# Revit family: QF_ELECTROLUXPROFESSIONAL_586243_PUET10KVEO
name_source: partatom
category: Specialty Equipment
revit_build: Autodesk Revit 2018 (Build: 20190510_1515(x64)
units: mm (PartAtom-declared; Revit-internal decimal feet)

## family parameters
Always vertical = Yes
Cut with Voids When Loaded = No
Part Type = Normal
Room Calculation Point = No
Round Connector Dimension = Use Radius
Shared = Yes
Work Plane-Based = No

## types (6) — shared parameters
50 Hertz Option = No
60 Hertz Option = Yes
Apparent Power = 0 VA
Cold Water Connection Height = 395 mm  [stored 1.29593 ft]
Cold Water Radius Size = 6.35 mm  [stored 0.0208333 ft]
Cold Water Size = 1"
Conn Conduit = Yes
Cycle = 60 Hz
Depth = 900 mm  [stored 2.95276 ft]
Direct Waste Size = 1"
Elec Conn Connection Height = 450 mm  [stored 1.47638 ft]
Electrical Remarks = 3PH+N 50/60HZ COMPATIBLE
FL Amps = 0 A
HP = 27.6 HP
Height = 900 mm  [stored 2.95276 ft]
Hot Water Connection Height = 395 mm  [stored 1.29593 ft]
Hot Water Flow = 0 GPM
Hot Water Radius Size = 6.35 mm  [stored 0.0208333 ft]
Hot Water Size = 1"
Indirect Waste Radius Size = 12.7 mm  [stored 0.0416667 ft]
Indirect Waste Size = 1"
Manufacturer = ELECTROLUX
Max Overcurrent Protection = 5 A
Min Ckt Ampacity = 0 A
Phase = 3
Plumbing Remarks = For Domestic Water Connection
URL = www.electrolux.com/foodservice
URL Cutsheet = www.electrolux.com/foodservice
URL Manufacturer = www.electrolux.com/foodservice
Volts = 400 V
Watts = 0 W
Weight = 320 kg
Width = 1600 mm  [stored 5.24934 ft]
zero-valued in all types: Code, Indirect Waste Connection Height

## per-type parameters (varying)
| type | Base Height | Description | Model |
| 586243_EL. TILTING PRESS. BRAIS. PAN+STEAM+CTS_100L_WALL MOUNTED | 500 mm  [stored 1.64042 ft] | High Productivity Cooking Electric Tilting Pressure Braising Pan-100lt Wall Mounted with CTS | 586243 |
| 586242_EL. TILTING PRESS. BRAIS. PAN+STEAM+CTS_100L(S) | 100 mm  [stored 0.328084 ft] | High Productivity Cooking Electric Tilting Pressure Braising Pan-100lt Freestanding with CTS | 586242 |
| 586241_EL. TILTING PRESS. BRAIS. PAN+STEAM+CTS_100L(H) | 200 mm  [stored 0.656168 ft] | High Productivity Cooking Electric Tilting Pressure Braising Pan-100lt Hygienic Profile-Freestanding with CTS | 586241 |
| 586240_EL. TILTING PRESS. BRAIS. PAN+STEAM_100L_WALL MOUNTED | 500 mm  [stored 1.64042 ft] | High Productivity Cooking Electric Tilting Pressure Braising Pan-100lt Wall Mounted | 586240 |
| 586239_EL. TILTING PRESS. BRAIS. PAN+STEAM_100L(S)_FS | 100 mm  [stored 0.328084 ft] | High Productivity Cooking Electric Tilting Pressure Braising Pan-100lt Freestanding | 586239 |
| 586238_EL. TILTING PRESS. BRAIS. PAN+STEAM_100L(H)_FS | 200 mm  [stored 0.656168 ft] | High Productivity Cooking Electric Tilting Pressure Braising Pan-100lt Hygienic Profile-Freestanding | 586238 |

note: [stored X ft] marks values corroborated as IEEE doubles in the binary element streams (Revit-internal decimal feet)

## geometry (parser evidence)
native form markers: Blend x27, Sweep x2
no freeform markers — native parametric forms only
